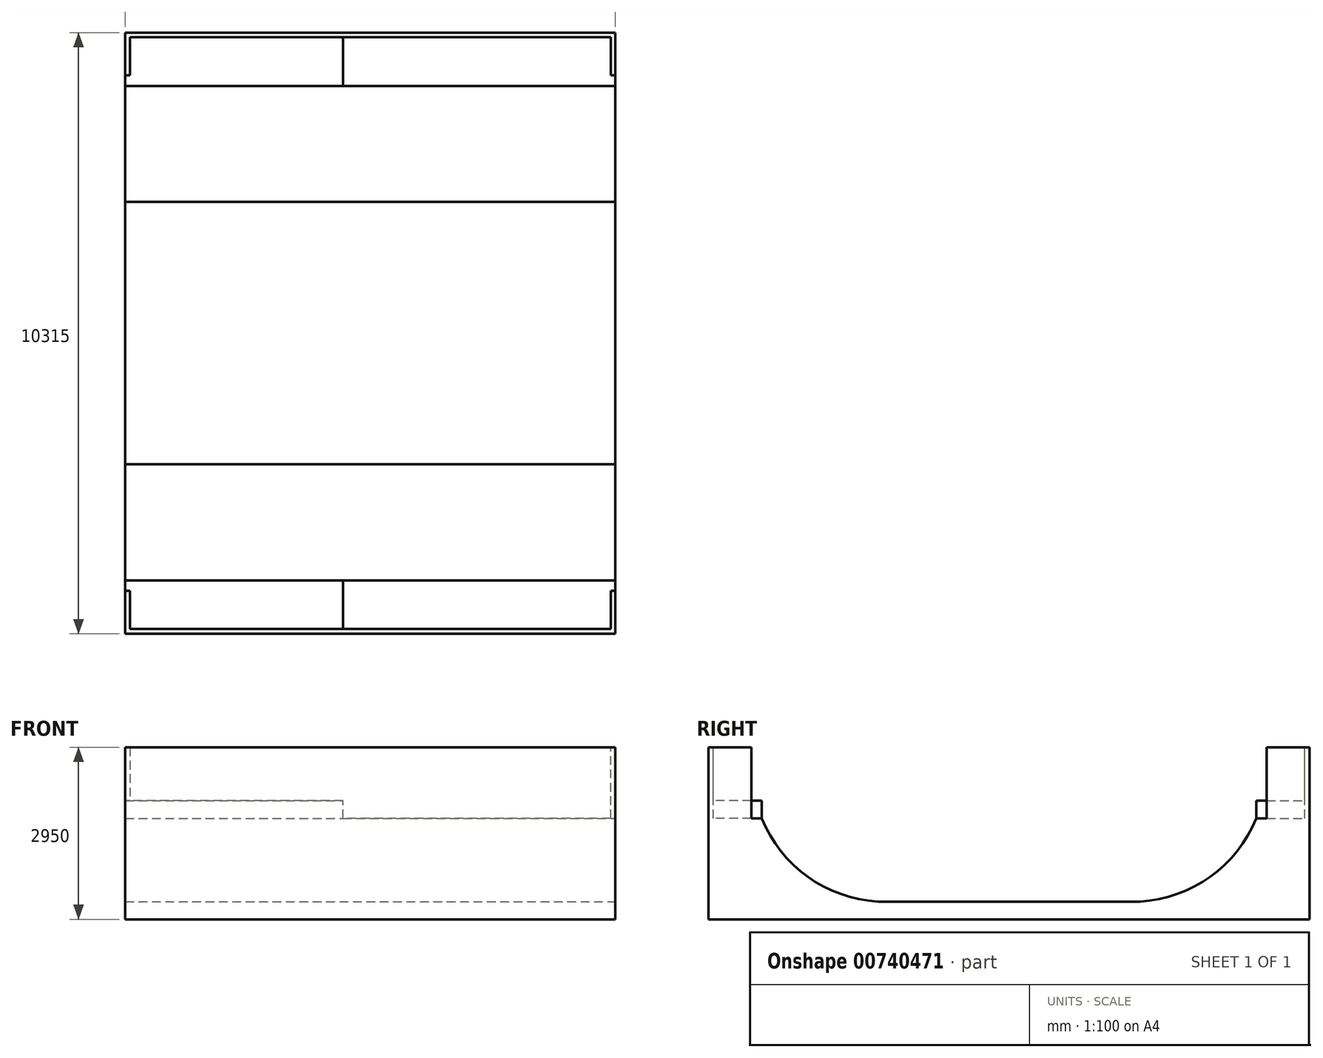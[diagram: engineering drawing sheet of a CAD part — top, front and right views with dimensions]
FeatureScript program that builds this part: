
annotation { "Feature Type Name" : "Feature", "Feature Type Description" : "" }
export const myFeature = defineFeature(function(context is Context, id is Id, definition is map)
    precondition{}
    {
        {
            var Q0;
            Q0=qCreatedBy(makeId("Top.planeOp"),FACE);
            var sketch = newSketch(context, id + "F0", { "sketchPlane" : qUnion([Q0])});
            skLineSegment(sketch, "E0.bottom", {"start": v(4207.5, 5157.5) * mm, "end": v(-4207.5, 5157.5) * mm});
            skLineSegment(sketch, "E0.top", {"start": v(4207.5, -5157.5) * mm, "end": v(-4207.5, -5157.5) * mm});
            skLineSegment(sketch, "E0.left", {"start": v(4207.5, 5157.5) * mm, "end": v(4207.5, -5157.5) * mm});
            skLineSegment(sketch, "E0.right", {"start": v(-4207.5, 5157.5) * mm, "end": v(-4207.5, -5157.5) * mm});
            skPoint(sketch, "E0.middle", {"position": v(0, 0) * mm});
            skLineSegment(sketch, "E1.bottom", {"start": v(4127.5, 5077.5) * mm, "end": v(-4127.5, 5077.5) * mm});
            skLineSegment(sketch, "E1.top", {"start": v(4127.5, -5077.5) * mm, "end": v(-4127.5, -5077.5) * mm});
            skLineSegment(sketch, "E1.left", {"start": v(4127.5, 5077.5) * mm, "end": v(4127.5, -5077.5) * mm});
            skLineSegment(sketch, "E1.right", {"start": v(-4127.5, 5077.5) * mm, "end": v(-4127.5, -5077.5) * mm});
            skLineSegment(sketch, "E2", {"start": v(-4127.5, -4243.1) * mm, "end": v(-4207.5, -4243.1) * mm});
            skLineSegment(sketch, "E3", {"start": v(4127.5, -4243.1) * mm, "end": v(4207.5, -4243.1) * mm});
            skLineSegment(sketch, "E4", {"start": v(-4207.5, 4243.1) * mm, "end": v(-4127.5, 4243.1) * mm});
            skLineSegment(sketch, "E5", {"start": v(4127.5, 4243.1) * mm, "end": v(4207.5, 4243.1) * mm});
            skLineSegment(sketch, "E6", {"start": v(-4127.5, 4243.1) * mm, "end": v(-469.9, 4243.1) * mm});
            skLineSegment(sketch, "E7", {"start": v(-469.9, 4243.1) * mm, "end": v(-469.9, 5077.5) * mm});
            skLineSegment(sketch, "E8", {"start": v(-469.9, 5077.5) * mm, "end": v(-469.9, -5077.5) * mm});
            skLineSegment(sketch, "E9", {"start": v(-4127.5, -4243.1) * mm, "end": v(-469.9, -4243.1) * mm});
            skSolve(sketch);
        }
        {
            var Q0;
            {var subQ2=sQuery(id+"F0.wireOp",EDGE,"E6");Q0=makeQuery(id+"F0.imprint","IMPRINT",FACE,{"disambiguationData":[TD([[makeQuery(id+"F0.imprint","IMPRINT",EDGE,{"derivedFrom":subQ2}),-1.0]])]});}
            var Q1;
            {var subQ0=sQuery(id+"F0.wireOp",EDGE,"E2");Q1=makeQuery(id+"F0.imprint","IMPRINT",FACE,{"disambiguationData":[TD([[makeQuery(id+"F0.imprint","IMPRINT",EDGE,{"derivedFrom":subQ0}),-1.0]])]});}
            var Q2;
            {var subQ0=sQuery(id+"F0.wireOp",EDGE,"E1.left");var subQ1=sQuery(id+"F0.wireOp",EDGE,"E1.bottom");var subQ2=makeQuery(id+"F0.imprint","INTERSECT",VERTEX,{"derivedFrom":[subQ1,subQ0]});Q2=makeQuery(id+"F0.imprint","IMPRINT",FACE,{"disambiguationData":[TD([[makeQuery(id+"F0.imprint","IMPRINT",EDGE,{"disambiguationData":[TD([[subQ2,-1.0]])],"derivedFrom":subQ1}),1.0]])]});}
            var Q3;
            {var subQ0=sQuery(id+"F0.wireOp",EDGE,"E3");Q3=makeQuery(id+"F0.imprint","IMPRINT",FACE,{"disambiguationData":[TD([[makeQuery(id+"F0.imprint","IMPRINT",EDGE,{"derivedFrom":subQ0}),1.0]])]});}
            var Q4;
            {var subQ5=sQuery(id+"F0.wireOp",EDGE,"E6");Q4=makeQuery(id+"F0.imprint","IMPRINT",FACE,{"disambiguationData":[TD([[makeQuery(id+"F0.imprint","IMPRINT",EDGE,{"derivedFrom":subQ5}),1.0]])]});}
            var Q5;
            {var subQ5=sQuery(id+"F0.wireOp",EDGE,"E0.bottom");Q5=makeQuery(id+"F0.imprint","IMPRINT",FACE,{"disambiguationData":[TD([[makeQuery(id+"F0.imprint","IMPRINT",EDGE,{"derivedFrom":subQ5}),1.0]])]});}
            var Q6;
            {var subQ5=sQuery(id+"F0.wireOp",EDGE,"E9");Q6=makeQuery(id+"F0.imprint","IMPRINT",FACE,{"disambiguationData":[TD([[makeQuery(id+"F0.imprint","IMPRINT",EDGE,{"derivedFrom":subQ5}),-1.0]])]});}
            var Q7;
            {var subQ5=sQuery(id+"F0.wireOp",EDGE,"E0.top");Q7=makeQuery(id+"F0.imprint","IMPRINT",FACE,{"disambiguationData":[TD([[makeQuery(id+"F0.imprint","IMPRINT",EDGE,{"derivedFrom":subQ5}),-1.0]])]});}
            extrude(context, id + "F1", {"entities" : qUnion([Q0, Q1, Q2, Q3, Q4, Q5, Q6, Q7]), "oppositeDirection" : true, "depth" : 2950 * mm, "offsetDistance" : 25 * mm});
        }
        {
            var Q0;
            {var subQ0=sQuery(id+"F0.wireOp",EDGE,"E2");Q0=makeQuery(id+"F0.imprint","IMPRINT",FACE,{"disambiguationData":[TD([[makeQuery(id+"F0.imprint","IMPRINT",EDGE,{"derivedFrom":subQ0}),-1.0]])]});}
            var Q1;
            {var subQ2=sQuery(id+"F0.wireOp",EDGE,"E6");Q1=makeQuery(id+"F0.imprint","IMPRINT",FACE,{"disambiguationData":[TD([[makeQuery(id+"F0.imprint","IMPRINT",EDGE,{"derivedFrom":subQ2}),-1.0]])]});}
            var Q2;
            {var subQ0=sQuery(id+"F0.wireOp",EDGE,"E1.left");var subQ1=sQuery(id+"F0.wireOp",EDGE,"E1.bottom");var subQ2=makeQuery(id+"F0.imprint","INTERSECT",VERTEX,{"derivedFrom":[subQ1,subQ0]});Q2=makeQuery(id+"F0.imprint","IMPRINT",FACE,{"disambiguationData":[TD([[makeQuery(id+"F0.imprint","IMPRINT",EDGE,{"disambiguationData":[TD([[subQ2,-1.0]])],"derivedFrom":subQ1}),1.0]])]});}
            var Q3;
            {var subQ0=sQuery(id+"F0.wireOp",EDGE,"E3");Q3=makeQuery(id+"F0.imprint","IMPRINT",FACE,{"disambiguationData":[TD([[makeQuery(id+"F0.imprint","IMPRINT",EDGE,{"derivedFrom":subQ0}),1.0]])]});}
            extrude(context, id + "F2", {"entities" : qUnion([Q0, Q1, Q2, Q3]), "operationType" : NewBodyOperationType.REMOVE, "oppositeDirection" : true, "depth" : 1219.2 * mm, "offsetDistance" : 25 * mm});
        }
        {
            var Q0;
            {var subQ5=sQuery(id+"F0.wireOp",EDGE,"E9");Q0=makeQuery(id+"F0.imprint","IMPRINT",FACE,{"disambiguationData":[TD([[makeQuery(id+"F0.imprint","IMPRINT",EDGE,{"derivedFrom":subQ5}),-1.0]])]});}
            var Q1;
            {var subQ5=sQuery(id+"F0.wireOp",EDGE,"E6");Q1=makeQuery(id+"F0.imprint","IMPRINT",FACE,{"disambiguationData":[TD([[makeQuery(id+"F0.imprint","IMPRINT",EDGE,{"derivedFrom":subQ5}),1.0]])]});}
            extrude(context, id + "F3", {"entities" : qUnion([Q0, Q1]), "operationType" : NewBodyOperationType.REMOVE, "oppositeDirection" : true, "depth" : 914.4 * mm, "offsetDistance" : 25 * mm});
        }
        {
            var Q0;
            Q0=makeQuery(id+"F1.opExtrude","SWEPT_FACE",FACE,{"disambiguationData":[OSD([sQuery(id+"F0.wireOp",EDGE,"E0.left")])]});
            var sketch = newSketch(context, id + "F4", { "sketchPlane" : qUnion([Q0])});
            skArc(sketch, "E10", {"start": v(-4243.1, -1219.2) * mm, "mid": v(-3453.9, -2221.78) * mm, "end": v(-2250.25, -2645.2) * mm});
            skLineSegment(sketch, "E11", {"start": v(-5157.5, -2645.2) * mm, "end": v(5157.5, -2645.2) * mm});
            skArc(sketch, "E12", {"start": v(2250.25, -2645.2) * mm, "mid": v(3453.9, -2221.78) * mm, "end": v(4243.1, -1219.2) * mm});
            skLineSegment(sketch, "E13.0", {"start": v(-4243.1, -1219.2) * mm, "end": v(-4243.1, 0) * mm});
            skLineSegment(sketch, "E13.1", {"start": v(4243.1, -1219.2) * mm, "end": v(-4243.1, -1219.2) * mm});
            skLineSegment(sketch, "E13.2", {"start": v(4243.1, -1219.2) * mm, "end": v(4243.1, 0) * mm});
            skLineSegment(sketch, "E14", {"start": v(-4243.1, -1219.2) * mm, "end": v(-4423.1, -1219.2) * mm});
            skLineSegment(sketch, "E15", {"start": v(-4423.1, -1219.2) * mm, "end": v(-4423.1, 0) * mm});
            skLineSegment(sketch, "E16", {"start": v(-4423.1, 0) * mm, "end": v(4423.1, 0) * mm});
            skLineSegment(sketch, "E17", {"start": v(4423.1, 0) * mm, "end": v(4423.1, -1219.2) * mm});
            skLineSegment(sketch, "E18", {"start": v(4423.1, -1219.2) * mm, "end": v(4243.1, -1219.2) * mm});
            skSolve(sketch);
        }
        {
            var Q0;
            {var subQ0=sQuery(id+"F4.wireOp",EDGE,"E10");Q0=makeQuery(id+"F4.imprint","IMPRINT",FACE,{"disambiguationData":[TD([[makeQuery(id+"F4.imprint","IMPRINT",EDGE,{"derivedFrom":subQ0}),1.0]])]});}
            extrude(context, id + "F5", {"entities" : qUnion([Q0]), "operationType" : NewBodyOperationType.REMOVE, "endBound" : BoundingType.THROUGH_ALL, "oppositeDirection" : true, "depth" : 25 * mm, "offsetDistance" : 25 * mm});
        }
        {
            var Q0;
            {var subQ0=sQuery(id+"F4.wireOp",EDGE,"E13.0");Q0=makeQuery(id+"F4.imprint","IMPRINT",FACE,{"disambiguationData":[TD([[makeQuery(id+"F4.imprint","IMPRINT",EDGE,{"derivedFrom":subQ0}),1.0]])]});}
            var Q1;
            {var subQ0=sQuery(id+"F4.wireOp",EDGE,"E13.2");Q1=makeQuery(id+"F4.imprint","IMPRINT",FACE,{"disambiguationData":[TD([[makeQuery(id+"F4.imprint","IMPRINT",EDGE,{"derivedFrom":subQ0}),-1.0]])]});}
            extrude(context, id + "F6", {"entities" : qUnion([Q0, Q1]), "operationType" : NewBodyOperationType.REMOVE, "endBound" : BoundingType.UP_TO_NEXT, "oppositeDirection" : true, "depth" : 25 * mm, "offsetDistance" : 25 * mm});
        }
        {
            var Q0;
            Q0=makeQuery(id+"F1.opExtrude","SWEPT_FACE",FACE,{"disambiguationData":[OSD([sQuery(id+"F0.wireOp",EDGE,"E0.right")])]});
            var sketch = newSketch(context, id + "F7", { "sketchPlane" : qUnion([Q0])});
            skLineSegment(sketch, "E19.0", {"start": v(-5077.5, 0) * mm, "end": v(5077.5, 0) * mm});
            skLineSegment(sketch, "E20.0", {"start": v(-4243.1, -914.4) * mm, "end": v(-4243.1, 0) * mm});
            skPoint(sketch, "E21.0", {"position": v(4243.1, -609.6) * mm});
            skLineSegment(sketch, "E22.0", {"start": v(4243.1, -914.4) * mm, "end": v(4243.1, 0) * mm});
            skLineSegment(sketch, "E23", {"start": v(-4423.1, -914.4) * mm, "end": v(-4423.1, 0) * mm});
            skLineSegment(sketch, "E24", {"start": v(4423.1, -914.4) * mm, "end": v(4423.1, 0) * mm});
            skPoint(sketch, "E25.0", {"position": v(-4243.1, -914.4) * mm});
            skLineSegment(sketch, "E26", {"start": v(-4243.1, -914.4) * mm, "end": v(-4423.1, -914.4) * mm});
            skPoint(sketch, "E27.orphan", {"position": v(-4243.1, -1219.2) * mm});
            skPoint(sketch, "E28.0", {"position": v(4243.1, -914.4) * mm});
            skLineSegment(sketch, "E29", {"start": v(4243.1, -914.4) * mm, "end": v(4423.1, -914.4) * mm});
            skPoint(sketch, "E30.orphan", {"position": v(4243.1, -1219.2) * mm});
            skSolve(sketch);
        }
        {
            var Q0;
            {var subQ0=sQuery(id+"F7.wireOp",EDGE,"E20.0");Q0=makeQuery(id+"F7.imprint","IMPRINT",FACE,{"disambiguationData":[TD([[makeQuery(id+"F7.imprint","IMPRINT",EDGE,{"derivedFrom":subQ0}),1.0]])]});}
            var Q1;
            {var subQ0=sQuery(id+"F7.wireOp",EDGE,"E22.0");Q1=makeQuery(id+"F7.imprint","IMPRINT",FACE,{"disambiguationData":[TD([[makeQuery(id+"F7.imprint","IMPRINT",EDGE,{"derivedFrom":subQ0}),-1.0]])]});}
            extrude(context, id + "F8", {"entities" : qUnion([Q0, Q1]), "operationType" : NewBodyOperationType.REMOVE, "endBound" : BoundingType.UP_TO_NEXT, "oppositeDirection" : true, "depth" : 25 * mm, "offsetDistance" : 25 * mm});
        }
    });
